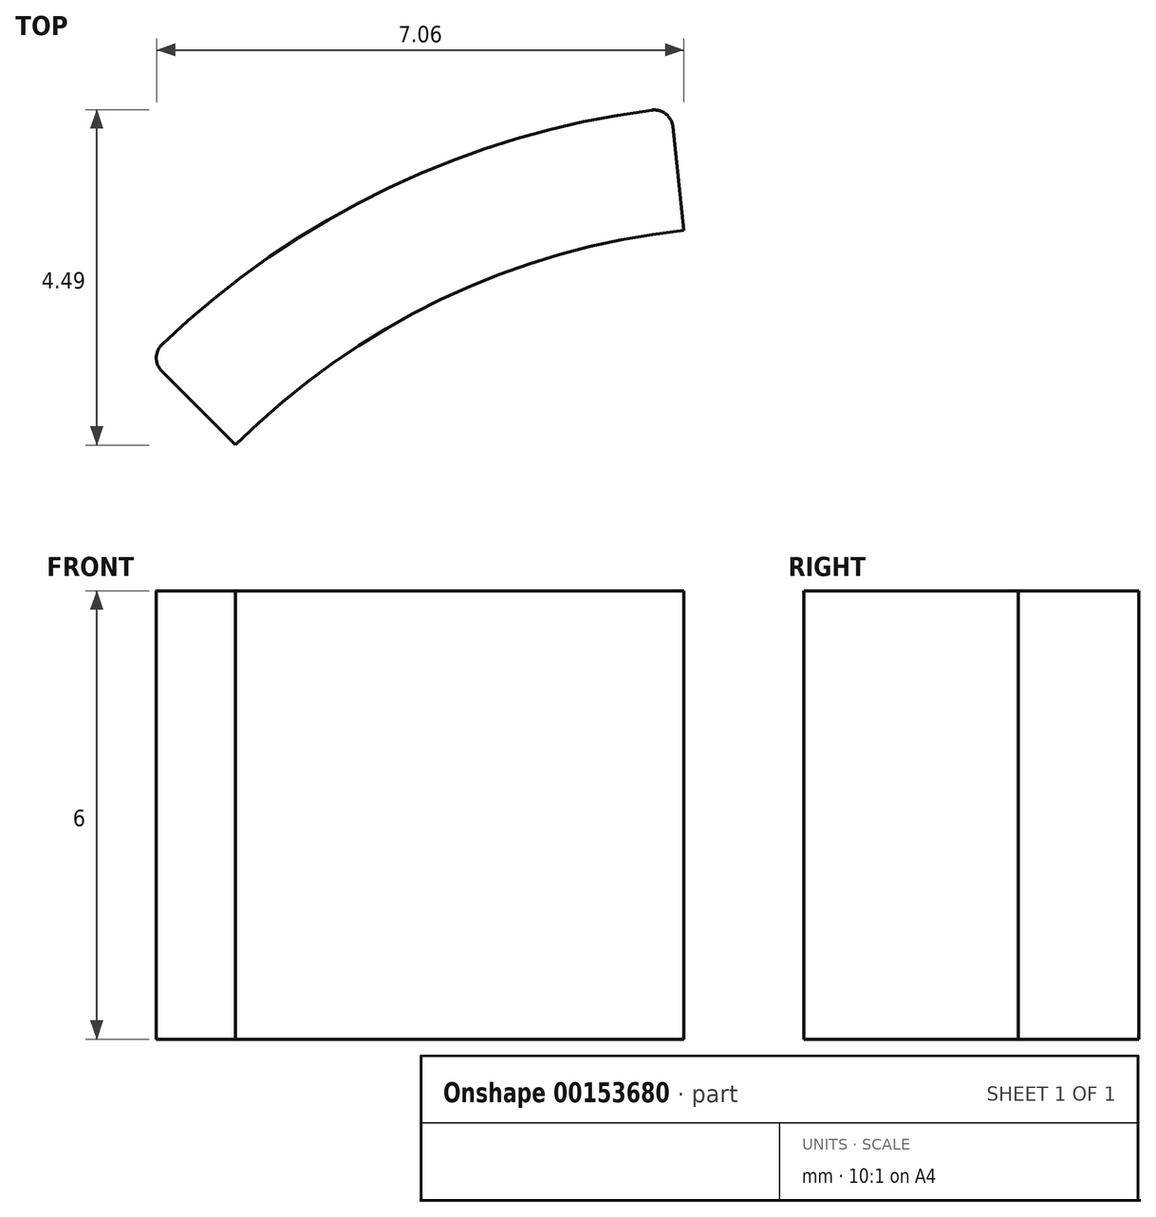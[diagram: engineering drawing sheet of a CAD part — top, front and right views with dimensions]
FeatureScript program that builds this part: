
annotation { "Feature Type Name" : "Feature", "Feature Type Description" : "" }
export const myFeature = defineFeature(function(context is Context, id is Id, definition is map)
    precondition{}
    {
        {
            var Q0;
            Q0=qCreatedBy(makeId("Top.planeOp"),FACE);
            var sketch = newSketch(context, id + "F0", { "sketchPlane" : qUnion([Q0])});
            skArc(sketch, "E0", {"start": v(0, 11.65) * mm, "mid": v(-0.62, 11.63) * mm, "end": v(-1.25, 11.58) * mm, "construction": true});
            skArc(sketch, "E1", {"start": v(0, 10) * mm, "mid": v(-0.54, 9.99) * mm, "end": v(-1.07, 9.94) * mm, "construction": true});
            skLineSegment(sketch, "E2", {"start": v(-8.06, 8.06) * mm, "end": v(-7.07, 7.07) * mm});
            skLineSegment(sketch, "E3", {"start": v(0, 11.65) * mm, "end": v(0, 10) * mm, "construction": true});
            skLineSegment(sketch, "E4", {"start": v(-1.22, 11.33) * mm, "end": v(-1.07, 9.94) * mm});
            skArc(sketch, "E5", {"start": v(-1.5, 11.55) * mm, "mid": v(-5.03, 10.5) * mm, "end": v(-8.06, 8.42) * mm});
            skArc(sketch, "E6", {"start": v(-1.07, 9.94) * mm, "mid": v(-4.32, 9.02) * mm, "end": v(-7.07, 7.07) * mm});
            skPoint(sketch, "E7.visualSharp", {"position": v(-8.24, 8.24) * mm});
            skArc(sketch, "E7.filletArc", {"start": v(-8.06, 8.42) * mm, "mid": v(-8.13, 8.24) * mm, "end": v(-8.06, 8.06) * mm});
            skPoint(sketch, "E8.visualSharp", {"position": v(-1.25, 11.58) * mm});
            skArc(sketch, "E8.filletArc", {"start": v(-1.22, 11.33) * mm, "mid": v(-1.31, 11.5) * mm, "end": v(-1.5, 11.55) * mm});
            skSolve(sketch);
        }
        {
            var Q0;
            Q0 = qSketchRegion(id + "F0", true);
            extrude(context, id + "F1", {"entities" : qUnion([Q0]), "depth" : 6 * mm});
        }
    });
